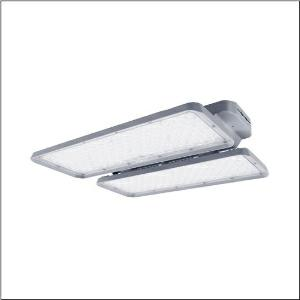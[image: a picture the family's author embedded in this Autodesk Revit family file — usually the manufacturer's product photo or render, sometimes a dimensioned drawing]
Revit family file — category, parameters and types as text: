
# Revit family: highbay_21-l_51hk41db4mca
name_source: partatom
category: Lighting Fixtures
units: mm (PartAtom-declared; Revit-internal decimal feet)

## family parameters
Cut with Voids When Loaded = No
Host = Face
Light Source = No
Part Type = Normal
Room Calculation Point = No
Round Connector Dimension = Use Diameter
Shared = No

## types (1)
- Highbay 21-L (1 x LED, 26200 lm, 147 W, 4000K)
    Apparent Load = 147 VA
    CIE Flux Codes = 87 97 99 100 100
    Color Rendering = 80
    Color Temperature = 4000K
    Default Elevation = 1800 mm
    Description = Highbay 21-L, LED high bay luminaire, primary light control with lens, of PC, light emission: direct distribution, primary light characteristic: symmetric, installation type: suspended mounting, surface-mounted, LED, rated luminous flux: 26.200lm, luminous efficacy: 180lm/W, light colour: 840, colour temperature: 4000K, with terminal, 5-pole, max. 2.5mm², mains connection: 220..240V, AC, 50Hz, rated input power: 147W, housing, of diecast aluminium, coated, grey, length: 471mm, width: 390mm, height: 87mm, protection rating (complete): IP66, insulation class (complete): insulation class I (protective earthing), certification: CE, ENEC, UKCA, protection symbol: D, impact resistance: IK08, permissible operating ambient temperature: -30..+60°C, corresponds to IFS (International Featured Standards) requirements for safety and quality in the food industry, LABS conformity tested according to VDMA 24364:2018-05, packaging unit: 1 piece
    Height = 89 mm
    Lamp = 1 x LED
    Lamp Light Flux = 26200 lm
    Lamp Power = 147 W
    Lamp count = 1
    Length = 471 mm
    Luminous efficacy = 178 lm/W
    Manufacturer = Siteco
    ModVariant = No
    Model = 51HK41DB4MCA
    Mounting Place = Ceiling
    Mounting Type = Pendant
    Number of Poles = 1
    OnlyDefault = Yes
    Power Factor = 1
    Product Name = Highbay 21-L
    Product group = LED high bay luminaire
    ProductGroupID = 903
    Protection Class = Protection class I
    Protection Degree = IP 66
    RLX_Detail_Level = 1
    RLX_Emergency_Light_Flux = 0 lm
    RLX_Emergency_Type = 0
    RLX_Emergency_Type_DB = No
    RlxData = <blob elided: 25425 chars, md5=c056d35b>
    Socket = socket
    Standby Power = 0 W
    System Light Flux = 26200 lm
    System Power = 147 W
    Type Comments = Product without accessories
    Type Image = l_1276530.jpg
    URL = http://relux.com
    VarID = ---
    Voltage = 0 V
    Weight = 0.00 kg
    Width = 390 mm

## geometry (parser evidence)
native form markers: Blend x4, Sweep x11
no freeform markers — native parametric forms only
